FCSTD DOCUMENT  (FreeCAD 1.0R38641 +468 (Git))
Label: forward_cuboid
License: All rights reserved
LicenseURL: https://en.wikipedia.org/wiki/All_rights_reserved
objects: Part::Part2DObjectPython×11
note: 11 computed .brp shape members not serialized (recipe doc carries the construction recipe); baked Part::Feature solids carry a one-line shape summary decoded from their .brp

FEATURE [Part::Part2DObjectPython] Line005  # Draft 2D object (typed FeaturePython)
  Area = 0
  ChamferSize = 0
  Closed = false
  End = (0,-20,0)
  FilletRadius = 0
  Length = 10
  MakeFace = true
  Placement = pos=(10,-20,0) rot=(0,0,1;0rad)
  Points = (2) [(0,0,0),(-10,0,0)]
  Start = (10,-20,0)
  Subdivisions = 0
FEATURE [Part::Part2DObjectPython] Line007  # Draft 2D object (typed FeaturePython)
  Area = 0
  ChamferSize = 0
  Closed = false
  End = (0,-10,0)
  FilletRadius = 0
  Length = 10
  MakeFace = true
  Placement = pos=(10,-10,0) rot=(0,0,1;0rad)
  Points = (2) [(0,0,0),(-10,0,0)]
  Start = (10,-10,0)
  Subdivisions = 0
FEATURE [Part::Part2DObjectPython] Line  # Draft 2D object (typed FeaturePython)
  Area = 0
  ChamferSize = 0
  Closed = false
  End = (-50,0,0)
  FilletRadius = 0
  Length = 50
  MakeFace = true
  Points = (2) [(0,0,0),(-50,0,0)]
  Start = (0,0,0)
  Subdivisions = 0
FEATURE [Part::Part2DObjectPython] Line015  # Draft 2D object (typed FeaturePython)
  Area = 0
  ChamferSize = 0
  Closed = false
  End = (0,10,0)
  FilletRadius = 0
  Length = 10
  MakeFace = true
  Placement = pos=(10,10,0) rot=(0,0,1;0rad)
  Points = (2) [(0,0,0),(-10,0,0)]
  Start = (10,10,0)
  Subdivisions = 0
FEATURE [Part::Part2DObjectPython] Line017  # Draft 2D object (typed FeaturePython)
  Area = 0
  ChamferSize = 0
  Closed = false
  End = (10,10,0)
  FilletRadius = 0
  Length = 10
  MakeFace = true
  Placement = pos=(10,0,0) rot=(0,0,1;0rad)
  Points = (2) [(0,0,0),(0,10,0)]
  Start = (10,0,0)
  Subdivisions = 0
FEATURE [Part::Part2DObjectPython] Line020  # Draft 2D object (typed FeaturePython)
  Area = 0
  ChamferSize = 0
  Closed = false
  End = (10,-10,0)
  FilletRadius = 0
  Length = 10
  MakeFace = true
  Placement = pos=(10,-20,0) rot=(0,0,1;0rad)
  Points = (2) [(0,0,0),(0,10,0)]
  Start = (10,-20,0)
  Subdivisions = 0
FEATURE [Part::Part2DObjectPython] Line022  # Draft 2D object (typed FeaturePython)
  Area = 0
  ChamferSize = 0
  Closed = false
  End = (50,0,0)
  FilletRadius = 0
  Length = 40
  MakeFace = true
  Placement = pos=(10,0,0) rot=(0,0,1;0rad)
  Points = (2) [(0,0,0),(40,0,0)]
  Start = (10,0,0)
  Subdivisions = 0
FEATURE [Part::Part2DObjectPython] Line024  # Draft 2D object (typed FeaturePython)
  Area = 0
  ChamferSize = 0
  Closed = false
  End = (10,-10,0)
  FilletRadius = 0
  Length = 10
  MakeFace = true
  Placement = pos=(10,0,0) rot=(0,0,1;0rad)
  Points = (2) [(0,0,0),(0,-10,0)]
  Start = (10,0,0)
  Subdivisions = 0
FEATURE [Part::Part2DObjectPython] Line027  # Draft 2D object (typed FeaturePython)
  Area = 0
  ChamferSize = 0
  Closed = false
  End = (0,-10,0)
  FilletRadius = 0
  Length = 10
  MakeFace = true
  Placement = pos=(0,-20,0) rot=(0,0,1;0rad)
  Points = (2) [(0,0,0),(0,10,0)]
  Start = (0,-20,0)
  Subdivisions = 0
FEATURE [Part::Part2DObjectPython] Line029  # Draft 2D object (typed FeaturePython)
  Area = 0
  ChamferSize = 0
  Closed = true
  End = (0,1,1e-16)
  FilletRadius = 0
  Length = 0
  MakeFace = true
  Placement = pos=(0,1,1e-16) rot=(0,0,1;0rad)
  Points = (2) [(0,0,0),(-3.7494e-33,0,0)]
  Start = (0,1,1e-16)
  Subdivisions = 0
FEATURE [Part::Part2DObjectPython] Line032  # Draft 2D object (typed FeaturePython)
  Area = 0
  ChamferSize = 0
  Closed = false
  End = (0,-10,0)
  FilletRadius = 0
  Length = 20
  MakeFace = true
  Placement = pos=(0,10,0) rot=(0,0,1;0rad)
  Points = (2) [(0,0,0),(0,-20,0)]
  Start = (0,10,0)
  Subdivisions = 0
